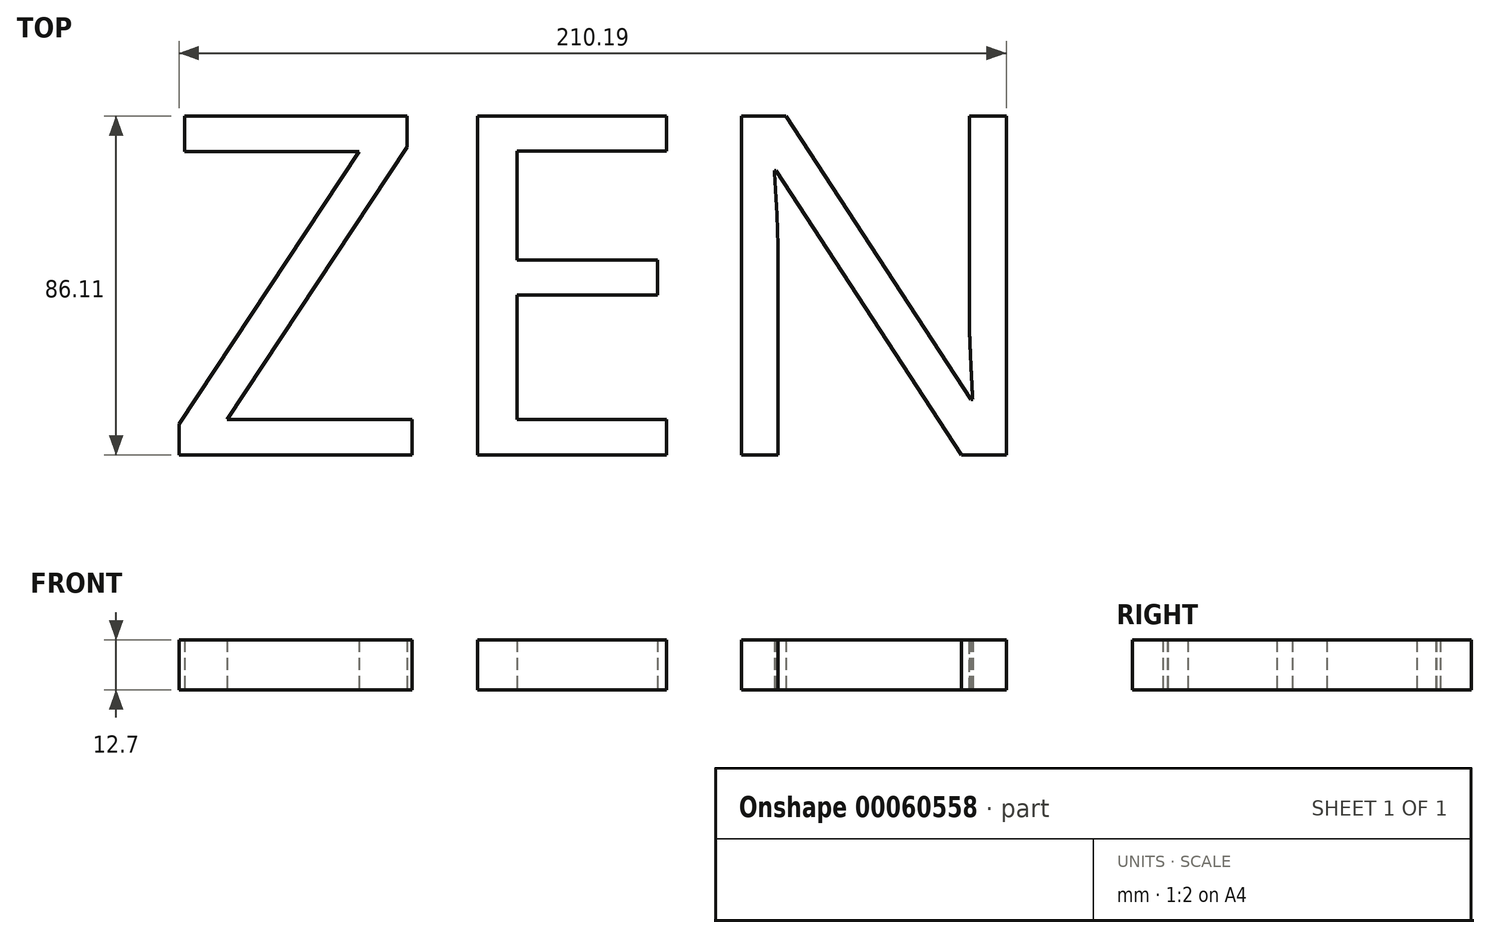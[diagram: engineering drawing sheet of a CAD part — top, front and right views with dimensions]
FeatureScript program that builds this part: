
annotation { "Feature Type Name" : "Feature", "Feature Type Description" : "" }
export const myFeature = defineFeature(function(context is Context, id is Id, definition is map)
    precondition{}
    {
        {
            var Q0;
            Q0=qCreatedBy(makeId("Top.planeOp"),FACE);
            var sketch = newSketch(context, id + "F0", { "sketchPlane" : qUnion([Q0])});
            skText(sketch, "E0", { "text": "ZEN", "fontName": "OpenSans-Regular.ttf"});
            const initialGuessF0  = {"E0": [0.00689, 0.03182, 1, 0, 0.08684]};
            skSetInitialGuess(sketch, initialGuessF0);
            skSolve(sketch);
        }
        {
            var Q0;
            Q0=makeQuery(id+"F0.imprint","IMPRINT",FACE,{"disambiguationData":[TD([[makeQuery(id+"F0.imprint","IMPRINT",EDGE,{"derivedFrom":sQuery(id+"F0.wireOp",EDGE,"E0.sketch_text.stroke-10")}),-1.0]])]});
            var Q1;
            Q1=makeQuery(id+"F0.imprint","IMPRINT",FACE,{"disambiguationData":[TD([[makeQuery(id+"F0.imprint","IMPRINT",EDGE,{"derivedFrom":sQuery(id+"F0.wireOp",EDGE,"E0.sketch_text.stroke-0")}),-1.0]])]});
            var Q2;
            Q2=makeQuery(id+"F0.imprint","IMPRINT",FACE,{"disambiguationData":[TD([[makeQuery(id+"F0.imprint","IMPRINT",EDGE,{"derivedFrom":sQuery(id+"F0.wireOp",EDGE,"E0.sketch_text.stroke-22")}),-1.0]])]});
            extrude(context, id + "F1", {"entities" : qUnion([Q0, Q1, Q2]), "depth" : 12.7 * mm});
        }
    });
